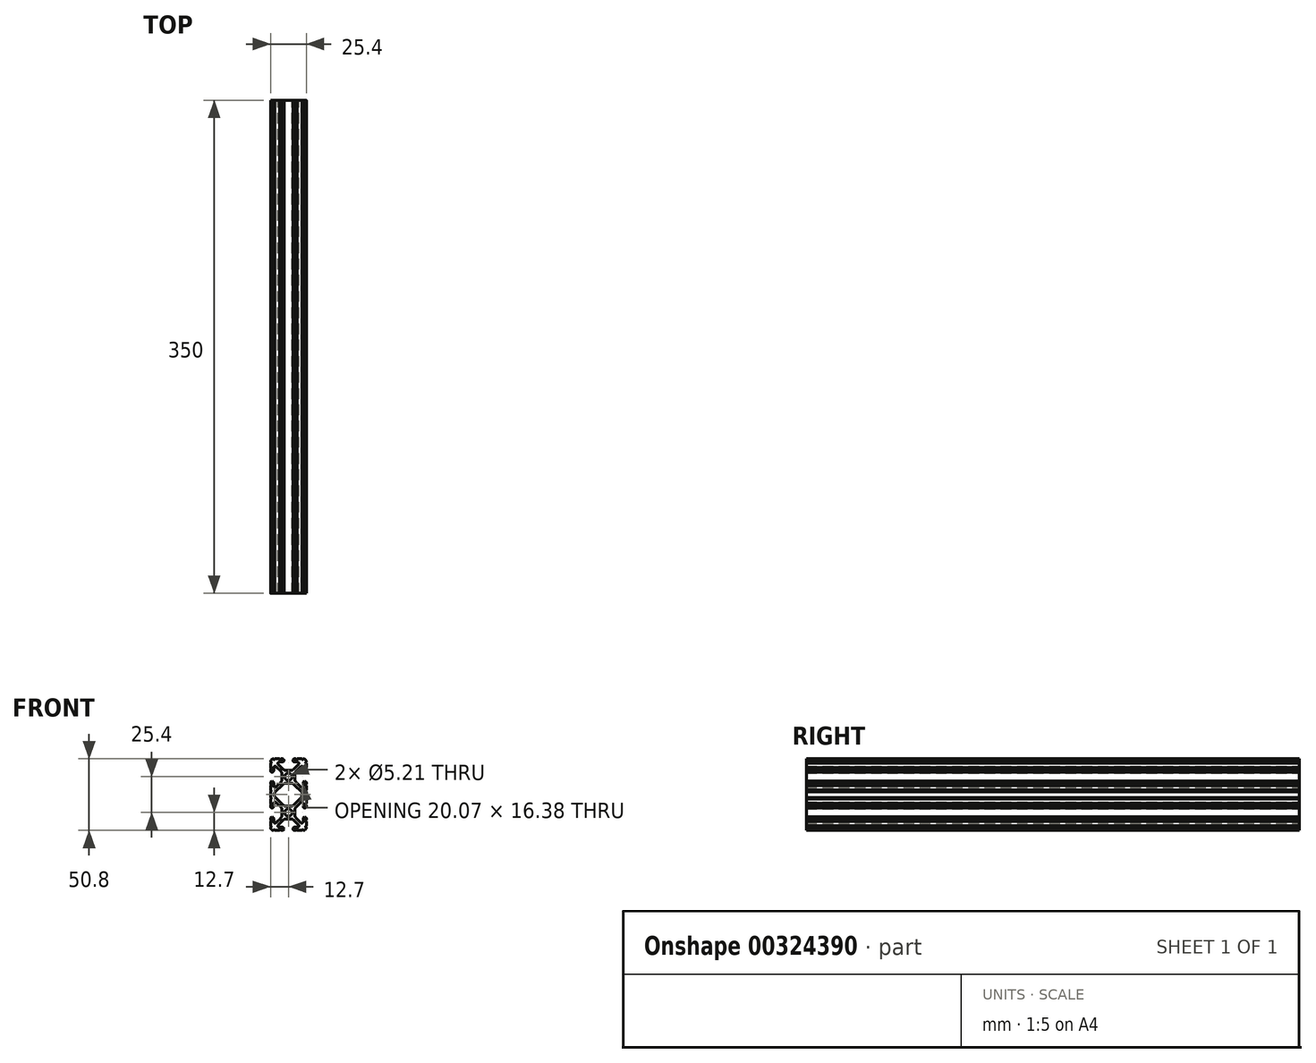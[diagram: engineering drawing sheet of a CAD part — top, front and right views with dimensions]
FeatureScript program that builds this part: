
annotation { "Feature Type Name" : "Feature", "Feature Type Description" : "" }
export const myFeature = defineFeature(function(context is Context, id is Id, definition is map)
    precondition{}
    {
        {
            var Q0;
            Q0=qCreatedBy(makeId("Front.planeOp"),FACE);
            var sketch = newSketch(context, id + "F0", { "sketchPlane" : qUnion([Q0])});
            skArc(sketch, "E0", {"start": v(2.6, -12.7) * mm, "mid": v(0, -10.1) * mm, "end": v(-2.6, -12.7) * mm});
            skArc(sketch, "E1", {"start": v(-2.6, -12.7) * mm, "mid": v(0, -15.3) * mm, "end": v(2.6, -12.7) * mm});
            skArc(sketch, "E2", {"start": v(-12.7, 22.25) * mm, "mid": v(-12.2, 22.76) * mm, "end": v(-12.7, 23.28) * mm});
            skLineSegment(sketch, "E3", {"start": v(-12.7, 22.25) * mm, "end": v(-12.7, 19.02) * mm});
            skArc(sketch, "E4", {"start": v(-12.7, 18) * mm, "mid": v(-12.2, 18.52) * mm, "end": v(-12.7, 19.02) * mm});
            skLineSegment(sketch, "E5", {"start": v(-12.7, 18) * mm, "end": v(-12.7, 17) * mm});
            skArc(sketch, "E6", {"start": v(-12.7, 17) * mm, "mid": v(-11.6, 15.9) * mm, "end": v(-10.5, 17) * mm});
            skLineSegment(sketch, "E7", {"start": v(-10.5, 17) * mm, "end": v(-10.5, 19.17) * mm});
            skArc(sketch, "E8", {"start": v(-8.76, 19.9) * mm, "mid": v(-9.86, 20.11) * mm, "end": v(-10.5, 19.17) * mm});
            skLineSegment(sketch, "E9", {"start": v(-8.76, 19.9) * mm, "end": v(-5.44, 16.58) * mm});
            skArc(sketch, "E10", {"start": v(-4.5, 14.33) * mm, "mid": v(-4.75, 15.55) * mm, "end": v(-5.44, 16.58) * mm});
            skLineSegment(sketch, "E11", {"start": v(-4.5, 14.33) * mm, "end": v(-4.5, 11.07) * mm});
            skArc(sketch, "E12", {"start": v(-5.44, 8.82) * mm, "mid": v(-4.75, 9.85) * mm, "end": v(-4.5, 11.07) * mm});
            skLineSegment(sketch, "E13", {"start": v(-5.44, 8.82) * mm, "end": v(-8.76, 5.5) * mm});
            skArc(sketch, "E14", {"start": v(-10.5, 6.23) * mm, "mid": v(-9.86, 5.29) * mm, "end": v(-8.76, 5.5) * mm});
            skLineSegment(sketch, "E15", {"start": v(-10.5, 6.23) * mm, "end": v(-10.5, 8.4) * mm});
            skArc(sketch, "E16", {"start": v(-10.5, 8.4) * mm, "mid": v(-11.6, 9.5) * mm, "end": v(-12.7, 8.4) * mm});
            skLineSegment(sketch, "E17", {"start": v(-12.7, 8.4) * mm, "end": v(-12.7, 7.4) * mm});
            skArc(sketch, "E18", {"start": v(-12.7, 6.38) * mm, "mid": v(-12.2, 6.88) * mm, "end": v(-12.7, 7.4) * mm});
            skLineSegment(sketch, "E19", {"start": v(-12.7, 6.38) * mm, "end": v(-12.7, 3.15) * mm});
            skArc(sketch, "E20", {"start": v(-12.7, 2.13) * mm, "mid": v(-12.2, 2.64) * mm, "end": v(-12.7, 3.15) * mm});
            skLineSegment(sketch, "E21", {"start": v(-12.7, 2.13) * mm, "end": v(-12.7, -2.13) * mm});
            skArc(sketch, "E22", {"start": v(-12.7, -3.15) * mm, "mid": v(-12.2, -2.64) * mm, "end": v(-12.7, -2.13) * mm});
            skLineSegment(sketch, "E23", {"start": v(-12.7, -3.15) * mm, "end": v(-12.7, -6.38) * mm});
            skArc(sketch, "E24", {"start": v(-12.7, -7.4) * mm, "mid": v(-12.2, -6.88) * mm, "end": v(-12.7, -6.38) * mm});
            skLineSegment(sketch, "E25", {"start": v(-12.7, -7.4) * mm, "end": v(-12.7, -8.4) * mm});
            skArc(sketch, "E26", {"start": v(-12.7, -8.4) * mm, "mid": v(-11.6, -9.5) * mm, "end": v(-10.5, -8.4) * mm});
            skLineSegment(sketch, "E27", {"start": v(-10.5, -8.4) * mm, "end": v(-10.5, -6.23) * mm});
            skArc(sketch, "E28", {"start": v(-8.76, -5.5) * mm, "mid": v(-9.86, -5.29) * mm, "end": v(-10.5, -6.23) * mm});
            skLineSegment(sketch, "E29", {"start": v(-8.76, -5.5) * mm, "end": v(-5.44, -8.82) * mm});
            skArc(sketch, "E30", {"start": v(-4.5, -11.07) * mm, "mid": v(-4.75, -9.85) * mm, "end": v(-5.44, -8.82) * mm});
            skLineSegment(sketch, "E31", {"start": v(-4.5, -11.07) * mm, "end": v(-4.5, -14.33) * mm});
            skArc(sketch, "E32", {"start": v(-5.44, -16.58) * mm, "mid": v(-4.75, -15.55) * mm, "end": v(-4.5, -14.33) * mm});
            skLineSegment(sketch, "E33", {"start": v(-5.44, -16.58) * mm, "end": v(-8.76, -19.9) * mm});
            skArc(sketch, "E34", {"start": v(-10.5, -19.17) * mm, "mid": v(-9.86, -20.11) * mm, "end": v(-8.76, -19.9) * mm});
            skLineSegment(sketch, "E35", {"start": v(-10.5, -19.17) * mm, "end": v(-10.5, -17) * mm});
            skArc(sketch, "E36", {"start": v(-10.5, -17) * mm, "mid": v(-11.6, -15.9) * mm, "end": v(-12.7, -17) * mm});
            skLineSegment(sketch, "E37", {"start": v(-12.7, -17) * mm, "end": v(-12.7, -18) * mm});
            skArc(sketch, "E38", {"start": v(-12.7, -19.02) * mm, "mid": v(-12.2, -18.52) * mm, "end": v(-12.7, -18) * mm});
            skLineSegment(sketch, "E39", {"start": v(-12.7, -19.02) * mm, "end": v(-12.7, -22.25) * mm});
            skArc(sketch, "E40", {"start": v(-12.7, -23.28) * mm, "mid": v(-12.2, -22.76) * mm, "end": v(-12.7, -22.25) * mm});
            skArc(sketch, "E41", {"start": v(-12.7, -23.28) * mm, "mid": v(-12.08, -24.78) * mm, "end": v(-10.58, -25.4) * mm});
            skArc(sketch, "E42", {"start": v(-9.55, -25.4) * mm, "mid": v(-10.06, -24.9) * mm, "end": v(-10.58, -25.4) * mm});
            skLineSegment(sketch, "E43", {"start": v(-9.55, -25.4) * mm, "end": v(-6.32, -25.4) * mm});
            skArc(sketch, "E44", {"start": v(-5.3, -25.4) * mm, "mid": v(-5.82, -24.9) * mm, "end": v(-6.32, -25.4) * mm});
            skLineSegment(sketch, "E45", {"start": v(-5.3, -25.4) * mm, "end": v(-4.3, -25.4) * mm});
            skArc(sketch, "E46", {"start": v(-4.3, -25.4) * mm, "mid": v(-3.2, -24.3) * mm, "end": v(-4.3, -23.2) * mm});
            skLineSegment(sketch, "E47", {"start": v(-4.3, -23.2) * mm, "end": v(-6.47, -23.2) * mm});
            skArc(sketch, "E48", {"start": v(-7.2, -21.46) * mm, "mid": v(-7.41, -22.56) * mm, "end": v(-6.47, -23.2) * mm});
            skLineSegment(sketch, "E49", {"start": v(-7.2, -21.46) * mm, "end": v(-3.88, -18.14) * mm});
            skArc(sketch, "E50", {"start": v(-1.63, -17.2) * mm, "mid": v(-2.85, -17.45) * mm, "end": v(-3.88, -18.14) * mm});
            skLineSegment(sketch, "E51", {"start": v(-1.63, -17.2) * mm, "end": v(1.63, -17.2) * mm});
            skArc(sketch, "E52", {"start": v(3.88, -18.14) * mm, "mid": v(2.85, -17.45) * mm, "end": v(1.63, -17.2) * mm});
            skLineSegment(sketch, "E53", {"start": v(3.88, -18.14) * mm, "end": v(7.2, -21.46) * mm});
            skArc(sketch, "E54", {"start": v(6.47, -23.2) * mm, "mid": v(7.41, -22.56) * mm, "end": v(7.2, -21.46) * mm});
            skLineSegment(sketch, "E55", {"start": v(6.47, -23.2) * mm, "end": v(4.3, -23.2) * mm});
            skArc(sketch, "E56", {"start": v(4.3, -23.2) * mm, "mid": v(3.2, -24.3) * mm, "end": v(4.3, -25.4) * mm});
            skLineSegment(sketch, "E57", {"start": v(4.3, -25.4) * mm, "end": v(5.3, -25.4) * mm});
            skArc(sketch, "E58", {"start": v(6.32, -25.4) * mm, "mid": v(5.82, -24.9) * mm, "end": v(5.3, -25.4) * mm});
            skLineSegment(sketch, "E59", {"start": v(6.32, -25.4) * mm, "end": v(9.55, -25.4) * mm});
            skArc(sketch, "E60", {"start": v(10.58, -25.4) * mm, "mid": v(10.06, -24.9) * mm, "end": v(9.55, -25.4) * mm});
            skArc(sketch, "E61", {"start": v(10.58, -25.4) * mm, "mid": v(12.08, -24.78) * mm, "end": v(12.7, -23.28) * mm});
            skArc(sketch, "E62", {"start": v(12.7, -22.25) * mm, "mid": v(12.2, -22.76) * mm, "end": v(12.7, -23.28) * mm});
            skLineSegment(sketch, "E63", {"start": v(12.7, -22.25) * mm, "end": v(12.7, -19.02) * mm});
            skArc(sketch, "E64", {"start": v(12.7, -18) * mm, "mid": v(12.2, -18.52) * mm, "end": v(12.7, -19.02) * mm});
            skLineSegment(sketch, "E65", {"start": v(12.7, -18) * mm, "end": v(12.7, -17) * mm});
            skArc(sketch, "E66", {"start": v(12.7, -17) * mm, "mid": v(11.6, -15.9) * mm, "end": v(10.5, -17) * mm});
            skLineSegment(sketch, "E67", {"start": v(10.5, -17) * mm, "end": v(10.5, -19.17) * mm});
            skArc(sketch, "E68", {"start": v(8.76, -19.9) * mm, "mid": v(9.86, -20.11) * mm, "end": v(10.5, -19.17) * mm});
            skLineSegment(sketch, "E69", {"start": v(8.76, -19.9) * mm, "end": v(5.44, -16.58) * mm});
            skArc(sketch, "E70", {"start": v(4.5, -14.33) * mm, "mid": v(4.75, -15.55) * mm, "end": v(5.44, -16.58) * mm});
            skLineSegment(sketch, "E71", {"start": v(4.5, -14.33) * mm, "end": v(4.5, -11.07) * mm});
            skArc(sketch, "E72", {"start": v(5.44, -8.82) * mm, "mid": v(4.75, -9.85) * mm, "end": v(4.5, -11.07) * mm});
            skLineSegment(sketch, "E73", {"start": v(5.44, -8.82) * mm, "end": v(8.76, -5.5) * mm});
            skArc(sketch, "E74", {"start": v(10.5, -6.23) * mm, "mid": v(9.86, -5.29) * mm, "end": v(8.76, -5.5) * mm});
            skLineSegment(sketch, "E75", {"start": v(10.5, -6.23) * mm, "end": v(10.5, -8.4) * mm});
            skArc(sketch, "E76", {"start": v(10.5, -8.4) * mm, "mid": v(11.6, -9.5) * mm, "end": v(12.7, -8.4) * mm});
            skLineSegment(sketch, "E77", {"start": v(12.7, -8.4) * mm, "end": v(12.7, -7.4) * mm});
            skArc(sketch, "E78", {"start": v(12.7, -6.38) * mm, "mid": v(12.2, -6.88) * mm, "end": v(12.7, -7.4) * mm});
            skLineSegment(sketch, "E79", {"start": v(12.7, -6.38) * mm, "end": v(12.7, -3.15) * mm});
            skArc(sketch, "E80", {"start": v(12.7, -2.13) * mm, "mid": v(12.2, -2.64) * mm, "end": v(12.7, -3.15) * mm});
            skLineSegment(sketch, "E81", {"start": v(12.7, -2.13) * mm, "end": v(12.7, 2.13) * mm});
            skArc(sketch, "E82", {"start": v(12.7, 3.15) * mm, "mid": v(12.2, 2.64) * mm, "end": v(12.7, 2.13) * mm});
            skLineSegment(sketch, "E83", {"start": v(12.7, 3.15) * mm, "end": v(12.7, 6.38) * mm});
            skArc(sketch, "E84", {"start": v(12.7, 7.4) * mm, "mid": v(12.2, 6.88) * mm, "end": v(12.7, 6.38) * mm});
            skLineSegment(sketch, "E85", {"start": v(12.7, 7.4) * mm, "end": v(12.7, 8.4) * mm});
            skArc(sketch, "E86", {"start": v(12.7, 8.4) * mm, "mid": v(11.6, 9.5) * mm, "end": v(10.5, 8.4) * mm});
            skLineSegment(sketch, "E87", {"start": v(10.5, 8.4) * mm, "end": v(10.5, 6.23) * mm});
            skArc(sketch, "E88", {"start": v(8.76, 5.5) * mm, "mid": v(9.86, 5.29) * mm, "end": v(10.5, 6.23) * mm});
            skLineSegment(sketch, "E89", {"start": v(8.76, 5.5) * mm, "end": v(5.44, 8.82) * mm});
            skArc(sketch, "E90", {"start": v(4.5, 11.07) * mm, "mid": v(4.75, 9.85) * mm, "end": v(5.44, 8.82) * mm});
            skLineSegment(sketch, "E91", {"start": v(4.5, 11.07) * mm, "end": v(4.5, 14.33) * mm});
            skArc(sketch, "E92", {"start": v(5.44, 16.58) * mm, "mid": v(4.75, 15.55) * mm, "end": v(4.5, 14.33) * mm});
            skLineSegment(sketch, "E93", {"start": v(5.44, 16.58) * mm, "end": v(8.76, 19.9) * mm});
            skArc(sketch, "E94", {"start": v(10.5, 19.17) * mm, "mid": v(9.86, 20.11) * mm, "end": v(8.76, 19.9) * mm});
            skLineSegment(sketch, "E95", {"start": v(10.5, 19.17) * mm, "end": v(10.5, 17) * mm});
            skArc(sketch, "E96", {"start": v(10.5, 17) * mm, "mid": v(11.6, 15.9) * mm, "end": v(12.7, 17) * mm});
            skLineSegment(sketch, "E97", {"start": v(12.7, 17) * mm, "end": v(12.7, 18) * mm});
            skArc(sketch, "E98", {"start": v(12.7, 19.02) * mm, "mid": v(12.2, 18.52) * mm, "end": v(12.7, 18) * mm});
            skLineSegment(sketch, "E99", {"start": v(12.7, 19.02) * mm, "end": v(12.7, 22.25) * mm});
            skArc(sketch, "E100", {"start": v(12.7, 23.28) * mm, "mid": v(12.2, 22.76) * mm, "end": v(12.7, 22.25) * mm});
            skArc(sketch, "E101", {"start": v(12.7, 23.28) * mm, "mid": v(12.08, 24.78) * mm, "end": v(10.58, 25.4) * mm});
            skArc(sketch, "E102", {"start": v(9.55, 25.4) * mm, "mid": v(10.06, 24.9) * mm, "end": v(10.58, 25.4) * mm});
            skLineSegment(sketch, "E103", {"start": v(9.55, 25.4) * mm, "end": v(6.32, 25.4) * mm});
            skArc(sketch, "E104", {"start": v(5.3, 25.4) * mm, "mid": v(5.82, 24.9) * mm, "end": v(6.32, 25.4) * mm});
            skLineSegment(sketch, "E105", {"start": v(5.3, 25.4) * mm, "end": v(4.3, 25.4) * mm});
            skArc(sketch, "E106", {"start": v(4.3, 25.4) * mm, "mid": v(3.2, 24.3) * mm, "end": v(4.3, 23.2) * mm});
            skLineSegment(sketch, "E107", {"start": v(4.3, 23.2) * mm, "end": v(6.47, 23.2) * mm});
            skArc(sketch, "E108", {"start": v(7.2, 21.46) * mm, "mid": v(7.41, 22.56) * mm, "end": v(6.47, 23.2) * mm});
            skLineSegment(sketch, "E109", {"start": v(7.2, 21.46) * mm, "end": v(3.88, 18.14) * mm});
            skArc(sketch, "E110", {"start": v(1.63, 17.2) * mm, "mid": v(2.85, 17.45) * mm, "end": v(3.88, 18.14) * mm});
            skLineSegment(sketch, "E111", {"start": v(1.63, 17.2) * mm, "end": v(-1.63, 17.2) * mm});
            skArc(sketch, "E112", {"start": v(-3.88, 18.14) * mm, "mid": v(-2.85, 17.45) * mm, "end": v(-1.63, 17.2) * mm});
            skLineSegment(sketch, "E113", {"start": v(-3.88, 18.14) * mm, "end": v(-7.2, 21.46) * mm});
            skArc(sketch, "E114", {"start": v(-6.47, 23.2) * mm, "mid": v(-7.41, 22.56) * mm, "end": v(-7.2, 21.46) * mm});
            skLineSegment(sketch, "E115", {"start": v(-6.47, 23.2) * mm, "end": v(-4.3, 23.2) * mm});
            skArc(sketch, "E116", {"start": v(-4.3, 23.2) * mm, "mid": v(-3.2, 24.3) * mm, "end": v(-4.3, 25.4) * mm});
            skLineSegment(sketch, "E117", {"start": v(-4.3, 25.4) * mm, "end": v(-5.3, 25.4) * mm});
            skArc(sketch, "E118", {"start": v(-6.32, 25.4) * mm, "mid": v(-5.82, 24.9) * mm, "end": v(-5.3, 25.4) * mm});
            skLineSegment(sketch, "E119", {"start": v(-6.32, 25.4) * mm, "end": v(-9.55, 25.4) * mm});
            skArc(sketch, "E120", {"start": v(-10.58, 25.4) * mm, "mid": v(-10.06, 24.9) * mm, "end": v(-9.55, 25.4) * mm});
            skArc(sketch, "E121", {"start": v(-10.58, 25.4) * mm, "mid": v(-12.08, 24.78) * mm, "end": v(-12.7, 23.28) * mm});
            skArc(sketch, "E122", {"start": v(2.6, 12.7) * mm, "mid": v(0, 15.3) * mm, "end": v(-2.6, 12.7) * mm});
            skArc(sketch, "E123", {"start": v(-2.6, 12.7) * mm, "mid": v(0, 10.1) * mm, "end": v(2.6, 12.7) * mm});
            skArc(sketch, "E124", {"start": v(-9.57, 1.57) * mm, "mid": v(-9.91, 1.05) * mm, "end": v(-10.03, 0.45) * mm});
            skLineSegment(sketch, "E125", {"start": v(-3.88, 7.26) * mm, "end": v(-9.57, 1.57) * mm});
            skArc(sketch, "E126", {"start": v(-1.63, 8.2) * mm, "mid": v(-2.85, 7.95) * mm, "end": v(-3.88, 7.26) * mm});
            skLineSegment(sketch, "E127", {"start": v(1.63, 8.2) * mm, "end": v(-1.63, 8.2) * mm});
            skArc(sketch, "E128", {"start": v(3.88, 7.26) * mm, "mid": v(2.85, 7.95) * mm, "end": v(1.63, 8.2) * mm});
            skLineSegment(sketch, "E129", {"start": v(9.57, 1.57) * mm, "end": v(3.88, 7.26) * mm});
            skArc(sketch, "E130", {"start": v(10.03, 0.45) * mm, "mid": v(9.91, 1.05) * mm, "end": v(9.57, 1.57) * mm});
            skLineSegment(sketch, "E131", {"start": v(10.03, -0.45) * mm, "end": v(10.03, 0.45) * mm});
            skArc(sketch, "E132", {"start": v(9.57, -1.57) * mm, "mid": v(9.91, -1.05) * mm, "end": v(10.03, -0.45) * mm});
            skLineSegment(sketch, "E133", {"start": v(3.88, -7.26) * mm, "end": v(9.57, -1.57) * mm});
            skArc(sketch, "E134", {"start": v(1.63, -8.2) * mm, "mid": v(2.85, -7.95) * mm, "end": v(3.88, -7.26) * mm});
            skLineSegment(sketch, "E135", {"start": v(-1.63, -8.2) * mm, "end": v(1.63, -8.2) * mm});
            skArc(sketch, "E136", {"start": v(-3.88, -7.26) * mm, "mid": v(-2.85, -7.95) * mm, "end": v(-1.63, -8.2) * mm});
            skLineSegment(sketch, "E137", {"start": v(-9.57, -1.57) * mm, "end": v(-3.88, -7.26) * mm});
            skArc(sketch, "E138", {"start": v(-10.03, -0.45) * mm, "mid": v(-9.91, -1.05) * mm, "end": v(-9.57, -1.57) * mm});
            skLineSegment(sketch, "E139", {"start": v(-10.03, 0.45) * mm, "end": v(-10.03, -0.45) * mm});
            skSolve(sketch);
        }
        {
            var Q0;
            Q0=makeQuery(id+"F0.imprint","IMPRINT",FACE,{"disambiguationData":[TD([[makeQuery(id+"F0.imprint","IMPRINT",EDGE,{"derivedFrom":sQuery(id+"F0.wireOp",EDGE,"E0")}),-1.0]])]});
            extrude(context, id + "F1", {"entities" : qUnion([Q0]), "depth" : 350 * mm});
        }
    });
